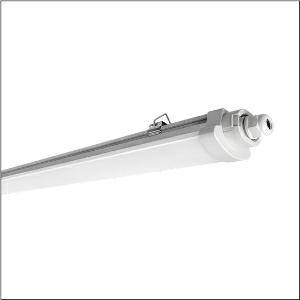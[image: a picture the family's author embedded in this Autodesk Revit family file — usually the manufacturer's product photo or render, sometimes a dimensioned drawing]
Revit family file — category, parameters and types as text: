
# Revit family: monsun_r__41_51fk20mn460a003_94ec
name_source: partatom
category: Lighting Fixtures
units: mm (PartAtom-declared; Revit-internal decimal feet)

## family parameters
Cut with Voids When Loaded = No
Host = Face
Light Source = No
Part Type = Normal
Room Calculation Point = No
Round Connector Dimension = Use Diameter
Shared = No

## types (1)
- --- (1 x LED, 6000 lm, 46 W, 4000K)
    Apparent Load = 46 VA
    CIE Flux Codes = 44 74 91 91 100
    Color Rendering = 80
    Color Temperature = 4000K
    Default Elevation = 1800 mm
    Description = Monsun® 41, damp-proof luminaire, primary optical cover: diffuser, of PC, frosted, light emission: direct distribution, primary light characteristic: symmetric, installation type: suspended mounting, surface-mounted, LED, rated luminous flux: 6.000lm, luminous efficacy: 130lm/W, light colour: 840, colour temperature: 4000K, control gear: ECG Multilumen, with terminal, 3-pole, through-wiring: 3x 1.5mm², mains connection: 220..240V, AC, 50/60Hz, rated input power: 46W, housing, luminaire housing, of PC, grey, length: 1.500mm, width: 79mm, height: 52mm, end cap, of PC, grey, ceiling mounting element, of stainless steel (V2A), protection rating (complete): IP65, insulation class (complete): insulation class II (safety insulation), certification: CE, UKCA, protection symbol: D, impact resistance: IK08, permissible operating ambient temperature: -20..+35°C, corresponds to IFS (International Featured Standards) requirements for safety and quality in the food industry, contact your sales advisor before using the luminaires in applications with unclear chemical exposure, large temperature fluctuations or condensation-forming humidity, packaging unit: 1 piece
    Height = 54 mm
    Lamp = 1 x LED
    Lamp Light Flux = 6000 lm
    Lamp Power = 46 W
    Lamp count = 1
    Length = 1500 mm
    Luminous efficacy = 130 lm/W
    Manufacturer = Siteco
    ModVariant = No
    Model = 51FK20MN460A003
    Mounting Place = Ceiling
    Mounting Type = Surface mounted
    Number of Poles = 1
    OnlyDefault = Yes
    Power Factor = 1
    Product Name = Monsun® 41
    Product group = damp-proof luminaire
    ProductGroupID = 300
    Protection Class = Protection class II
    Protection Degree = IP 65
    RLX_Detail_Level = 1
    RLX_Emergency_Light_Flux = 0 lm
    RLX_Emergency_Type = 0
    RLX_Emergency_Type_DB = No
    RlxData = <blob elided: 28829 chars, md5=8e9dfb07>
    Socket = socket
    Standby Power = 0 W
    System Light Flux = 6000 lm
    System Power = 46 W
    Type Comments = factory setting: luminous flux: 100 % | (HIGH)
    Type Image = l_1007037.jpg
    URL = http://relux.com
    VarID = @adj_107845
    Voltage = 0 V
    Weight = 0.00 kg
    Width = 79 mm

## geometry (parser evidence)
native form markers: Blend x4, Sweep x15
no freeform markers — native parametric forms only
